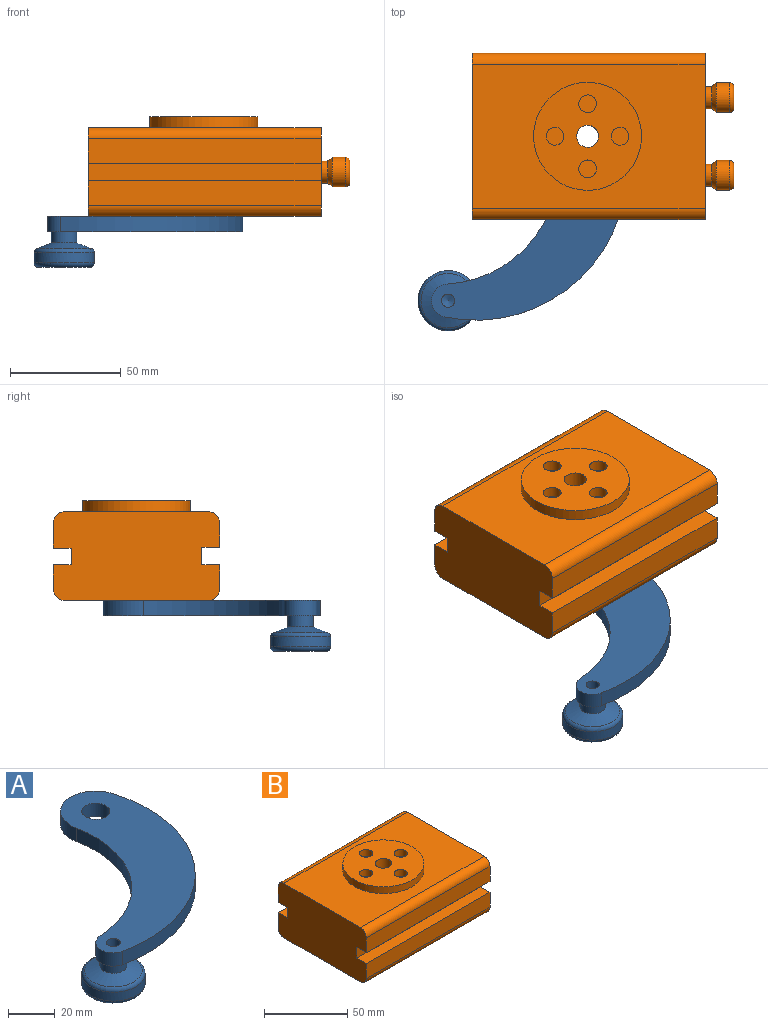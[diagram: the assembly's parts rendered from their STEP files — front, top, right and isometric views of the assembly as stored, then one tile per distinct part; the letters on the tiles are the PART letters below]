
ASSEMBLY  parts=2 mates=1
PART A: 15 faces, bbox 95.2x103.7x23 mm
  f0: cylinder r=53.23mm len=63.62mm, axis (0,0,-1), area 637.7mm2, adj f1,f4,f6,f7
  f1: cylinder r=7.5mm len=14.82mm, axis (0,0,-1), area 150.9mm2, adj f0,f2,f6,f7
  f2: cylinder r=67.99mm len=87.09mm, axis (0,0,-1), area 982.7mm2, adj f1,f4,f6,f7
  f3: cylinder r=6mm len=12mm, axis (0,0,-1), area 263.9mm2, adj f6,f7
  f4: cylinder r=15mm len=29.4mm, axis (0,0,-1), area 320.8mm2, adj f0,f2,f6,f7
  f5: cylinder r=3mm len=12mm, axis (0,0,-1), area 226.2mm2, adj f6,f10
  f6: plane 97.87x88.05mm, normal (0,0,1), area 3270.8mm2, adj f0,f1,f2,f3,f4,f5
  f7: plane 97.87x88.05mm, normal (0,0,-1), area 3195.6mm2, adj f0,f1,f2,f3,f4,f8
  f8: cylinder r=5.74mm len=11.47mm, axis (0,0,1), area 180.2mm2, adj f7,f9
  f9: cone r=5.74mm half-angle=69deg, axis (0,0,-1), area 395.8mm2, adj f8,f14
  f10: cone r=3mm half-angle=69deg, axis (0,0,1), area 30.3mm2, adj f5
  f11: cylinder r=13.55mm len=27.1mm, axis (0,0,1), area 393.9mm2, adj f13,f14
  f12: plane 23.1x23.1mm, normal (0,0,-1), area 419.3mm2, adj f13
  f13: torus R=11.55mm, axis (0,0,-1), area 253.2mm2, adj f11,f12
  f14: torus R=11.55mm, axis (0,0,1), area 198.3mm2, adj f9,f11
PART B: 43 faces, bbox 118x75x45 mm
  f0: plane 105x11mm, normal (0,-1,0), area 1155mm2, adj f1,f4,f13,f15
  f1: plane 75x40mm, normal (1,0,0), area 2697mm2, adj f0,f2,f3,f5,f7,f8,f9,f10
  f2: plane 105x11.39mm, normal (0,1,0), area 1195.5mm2, adj f1,f4,f9,f18
  f3: plane 105x11.06mm, normal (0,1,0), area 1161mm2, adj f1,f4,f10,f16
  f4: plane 75x40mm, normal (-1,0,0), area 2854.1mm2, adj f0,f2,f3,f5,f7,f8,f9,f10
  f5: plane 105x11mm, normal (0,-1,0), area 1155mm2, adj f1,f4,f12,f17
  f6: cylinder r=5mm len=45mm, axis (0,0,-1), area 1413.7mm2, adj f8,f38
  f7: plane 105x65mm, normal (0,0,1), area 4962mm2, adj f1,f4,f17,f18,f37
  f8: plane 105x65mm, normal (0,0,-1), area 6746.5mm2, adj f1,f4,f6,f15,f16
  f9: plane 105x8mm, normal (0,0,-1), area 840mm2, adj f1,f2,f4,f11
  f10: plane 105x8mm, normal (0,0,1), area 840mm2, adj f1,f3,f4,f11
  f11: plane 105x7.56mm, normal (0,1,0), area 793.5mm2, adj f1,f4,f9,f10
  f12: plane 105x8mm, normal (0,0,-1), area 840mm2, adj f1,f4,f5,f14
  f13: plane 105x8mm, normal (0,0,1), area 840mm2, adj f0,f1,f4,f14
  f14: plane 105x8mm, normal (0,-1,0), area 840mm2, adj f1,f4,f12,f13
  f15: cylinder r=5mm len=105mm, axis (1,0,0), area 824.7mm2, adj f0,f1,f4,f8
  f16: cylinder r=5mm len=105mm, axis (-1,0,0), area 824.7mm2, adj f1,f3,f4,f8
  f17: cylinder r=5mm len=105mm, axis (-1,0,0), area 824.7mm2, adj f1,f4,f5,f7
  f18: cylinder r=5mm len=105mm, axis (1,0,0), area 824.7mm2, adj f1,f2,f4,f7
  f19: cylinder r=5mm len=10mm, axis (-1,0,0), area 94.2mm2, adj f1,f21
  f20: cylinder r=5mm len=10mm, axis (-1,0,0), area 94.2mm2, adj f1,f22
  f21: cone r=5mm half-angle=40deg, axis (1,0,0), area 95.8mm2, adj f19,f23
  f22: cone r=5mm half-angle=40deg, axis (1,0,0), area 95.8mm2, adj f20,f25
  f23: cylinder r=6.68mm len=13.36mm, axis (-1,0,0), area 251.8mm2, adj f21,f32
  f24: plane 9.36x9.36mm, normal (1,0,0), area 40.5mm2, adj f29,f32
  f25: cylinder r=6.68mm len=13.36mm, axis (-1,0,0), area 251.8mm2, adj f22,f31
  f26: plane 9.36x9.36mm, normal (1,0,0), area 40.5mm2, adj f27,f31
  f27: cylinder r=3mm len=6mm, axis (1,0,0), area 94.2mm2, adj f26,f28
  f28: plane 6x6mm, normal (1,0,0), area 28.3mm2, adj f27
  f29: cylinder r=3mm len=6mm, axis (1,0,0), area 94.2mm2, adj f24,f30
  f30: plane 6x6mm, normal (1,0,0), area 28.3mm2, adj f29
  f31: torus R=4.68mm, axis (1,0,0), area 117.5mm2, adj f25,f26
  f32: torus R=4.68mm, axis (1,0,0), area 117.5mm2, adj f23,f24
  f33: cylinder r=4mm len=8mm, axis (0,0,-1), area 125.7mm2, adj f38,f42
  f34: cylinder r=4mm len=8mm, axis (0,0,-1), area 125.7mm2, adj f38,f41
  f35: cylinder r=4mm len=8mm, axis (0,0,-1), area 125.7mm2, adj f38,f40
  f36: cylinder r=4mm len=8mm, axis (0,0,-1), area 125.7mm2, adj f38,f39
  f37: cylinder r=24.35mm len=48.7mm, axis (0,0,-1), area 765mm2, adj f7,f38
  f38: plane 48.7x48.7mm, normal (0,0,1), area 1583.4mm2, adj f6,f33,f34,f35,f36,f37
  f39: plane 8x8mm, normal (0,0,1), area 50.3mm2, adj f36
  f40: plane 8x8mm, normal (0,0,1), area 50.3mm2, adj f35
  f41: plane 8x8mm, normal (0,0,1), area 50.3mm2, adj f34
  f42: plane 8x8mm, normal (0,0,1), area 50.3mm2, adj f33
PLACE A t=(-54.81,-56.01,-7.38)mm
PLACE B t=(24.4,-10.37,-10.38)mm
MATE fastened A.f3 <-> B.f8  axis (0,0,1) through (8.61,18.05,-0.38)mm
